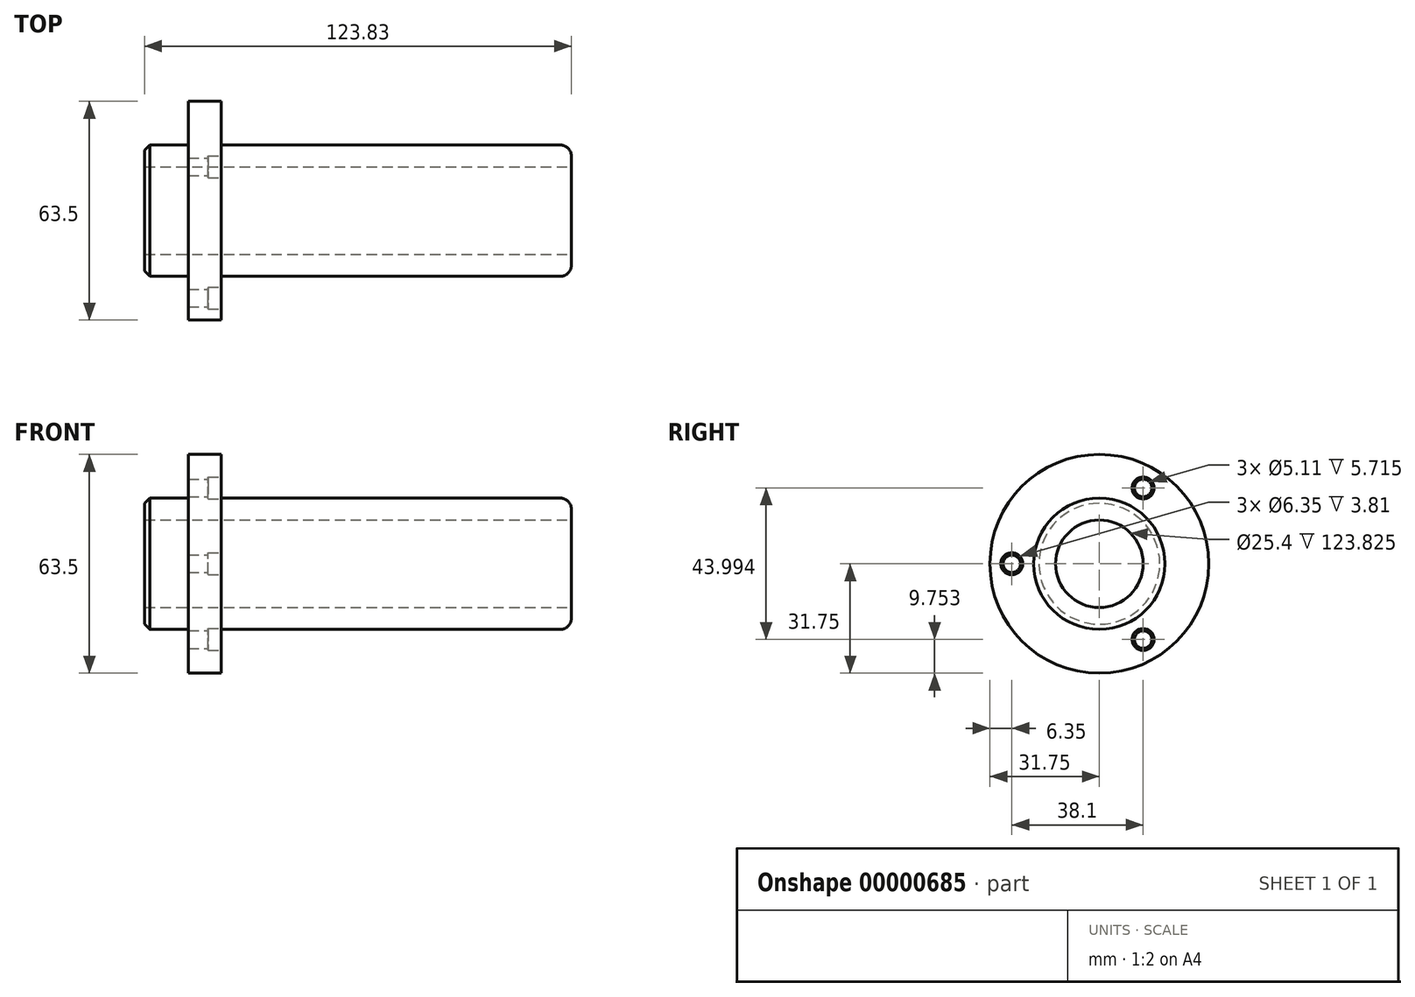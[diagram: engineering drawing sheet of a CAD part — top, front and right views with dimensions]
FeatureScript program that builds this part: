
annotation { "Feature Type Name" : "Feature", "Feature Type Description" : "" }
export const myFeature = defineFeature(function(context is Context, id is Id, definition is map)
    precondition{}
    {
        {
            var Q0;
            Q0=qCreatedBy(makeId("Front.planeOp"),FACE);
            var sketch = newSketch(context, id + "F0", { "sketchPlane" : qUnion([Q0])});
            skLineSegment(sketch, "E0", {"start": v(0, 0) * mm, "end": v(123.83, 0) * mm, "construction": true});
            skLineSegment(sketch, "E1", {"start": v(123.83, 0) * mm, "end": v(123.83, 15.88) * mm});
            skLineSegment(sketch, "E2", {"start": v(120.65, 19.05) * mm, "end": v(22.23, 19.05) * mm});
            skLineSegment(sketch, "E3", {"start": v(22.23, 19.05) * mm, "end": v(22.23, 31.75) * mm});
            skLineSegment(sketch, "E4", {"start": v(22.23, 31.75) * mm, "end": v(12.7, 31.75) * mm});
            skLineSegment(sketch, "E5", {"start": v(12.7, 31.75) * mm, "end": v(12.7, 19.05) * mm});
            skLineSegment(sketch, "E6", {"start": v(12.7, 19.05) * mm, "end": v(0, 19.05) * mm});
            skLineSegment(sketch, "E7", {"start": v(0, 19.05) * mm, "end": v(0, 0) * mm});
            skPoint(sketch, "E8.visualSharp", {"position": v(123.83, 19.05) * mm});
            skArc(sketch, "E8.filletArc", {"start": v(123.83, 15.88) * mm, "mid": v(122.9, 18.12) * mm, "end": v(120.65, 19.05) * mm});
            skLineSegment(sketch, "E9", {"start": v(0, 0) * mm, "end": v(123.83, 0) * mm});
            skSolve(sketch);
        }
        {
            var Q0;
            Q0=makeQuery(id+"F0.imprint","IMPRINT",FACE,{"disambiguationData":[TD([[makeQuery(id+"F0.imprint","IMPRINT",EDGE,{"derivedFrom":sQuery(id+"F0.wireOp",EDGE,"E1")}),1.0]])]});
            var Q1;
            Q1=sQuery(id+"F0.wireOp",EDGE,"E0");
            revolve(context, id + "F1", {"entities" : qUnion([Q0]), "axis" : qUnion([Q1]), "revolveType" : RevolveType.FULL});
        }
        {
            var Q0;
            Q0=makeQuery(id+"F1.opRevolve","SWEPT_EDGE",EDGE,{"disambiguationData":[OSD([sQuery(id+"F0.wireOp",EDGE,"E6"),sQuery(id+"F0.wireOp",EDGE,"E7")])]});
            chamfer(context, id + "F2", {"entities" : qUnion([Q0]), "chamferType" : ChamferType.OFFSET_ANGLE, "width" : 1.52 * mm, "oppositeDirection" : false, "angle" : 45 * degree, "tangentPropagation" : true});
        }
        {
            var Q0;
            Q0=makeQuery(id+"F1.opRevolve","SWEPT_FACE",FACE,{"disambiguationData":[OSD([sQuery(id+"F0.wireOp",EDGE,"E1")])]});
            var sketch = newSketch(context, id + "F3", { "sketchPlane" : qUnion([Q0])});
            skCircle(sketch, "E10", {"center": v(0, 0) * mm, "radius": 12.7 * mm});
            skSolve(sketch);
        }
        {
            var Q0;
            Q0=makeQuery(id+"F3.imprint","IMPRINT",FACE,{"disambiguationData":[TD([[makeQuery(id+"F3.imprint","IMPRINT",EDGE,{"derivedFrom":sQuery(id+"F3.wireOp",EDGE,"E10")}),1.0]])]});
            extrude(context, id + "F4", {"entities" : qUnion([Q0]), "operationType" : NewBodyOperationType.REMOVE, "endBound" : BoundingType.THROUGH_ALL, "oppositeDirection" : true, "depth" : 25.4 * mm});
        }
        {
            var Q0;
            Q0=makeQuery(id+"F1.opRevolve","SWEPT_FACE",FACE,{"disambiguationData":[OSD([sQuery(id+"F0.wireOp",EDGE,"E3")])]});
            var sketch = newSketch(context, id + "F5", { "sketchPlane" : qUnion([Q0])});
            skCircle(sketch, "E11", {"center": v(-25.4, 0) * mm, "radius": 3.18 * mm});
            skLineSegment(sketch, "E12", {"start": v(-25.4, 0) * mm, "end": v(0, 0) * mm, "construction": true});
            skSolve(sketch);
        }
        {
            var Q0;
            Q0=makeQuery(id+"F5.imprint","IMPRINT",FACE,{"disambiguationData":[TD([[makeQuery(id+"F5.imprint","IMPRINT",EDGE,{"derivedFrom":sQuery(id+"F5.wireOp",EDGE,"E11")}),1.0]])]});
            extrude(context, id + "F6", {"entities" : qUnion([Q0]), "operationType" : NewBodyOperationType.REMOVE, "oppositeDirection" : true, "depth" : 3.8 * mm});
        }
        {
            var Q0;
            Q0=makeQuery(id+"F6.boolean.opBoolean","COPY",FACE,{"derivedFrom":makeQuery(id+"F6.opExtrude","CAP_FACE",FACE,{"disambiguationData":[OSD([sQuery(id+"F5.wireOp",EDGE,"E11")])],"isStart":false})});
            var sketch = newSketch(context, id + "F7", { "sketchPlane" : qUnion([Q0])});
            skCircle(sketch, "E13", {"center": v(-25.4, 0) * mm, "radius": 2.55 * mm});
            skSolve(sketch);
        }
        {
            var Q0;
            Q0=makeQuery(id+"F7.imprint","IMPRINT",FACE,{"disambiguationData":[TD([[makeQuery(id+"F7.imprint","IMPRINT",EDGE,{"derivedFrom":sQuery(id+"F7.wireOp",EDGE,"E13")}),1.0]])]});
            extrude(context, id + "F8", {"entities" : qUnion([Q0]), "operationType" : NewBodyOperationType.REMOVE, "endBound" : BoundingType.THROUGH_ALL, "oppositeDirection" : true, "depth" : 25.4 * mm});
        }
        {
            var Q0;
            Q0=makeQuery(id+"F6.boolean.opBoolean","COPY",FACE,{"derivedFrom":makeQuery(id+"F6.opExtrude","SWEPT_FACE",FACE,{"disambiguationData":[OSD([sQuery(id+"F5.wireOp",EDGE,"E11")])]})});
            var Q1;
            Q1=makeQuery(id+"F6.boolean.opBoolean","COPY",FACE,{"derivedFrom":makeQuery(id+"F6.opExtrude","CAP_FACE",FACE,{"disambiguationData":[OSD([sQuery(id+"F5.wireOp",EDGE,"E11")])],"isStart":false})});
            var Q2;
            Q2=makeQuery(id+"F8.boolean.opBoolean","COPY",FACE,{"derivedFrom":makeQuery(id+"F8.opExtrude","SWEPT_FACE",FACE,{"disambiguationData":[OSD([sQuery(id+"F7.wireOp",EDGE,"E13")])]})});
            var Q3;
            Q3=makeQuery(id+"F1.opRevolve","SWEPT_FACE",FACE,{"disambiguationData":[OSD([sQuery(id+"F0.wireOp",EDGE,"E4")])]});
            circularPattern(context, id + "F9", {"faces" : qUnion([Q0, Q1, Q2]), "axis" : qUnion([Q3]), "angle" : 360 * degree, "instanceCount" : 3, "equalSpace" : true, "patternType" : PatternType.FACE});
        }
    });
